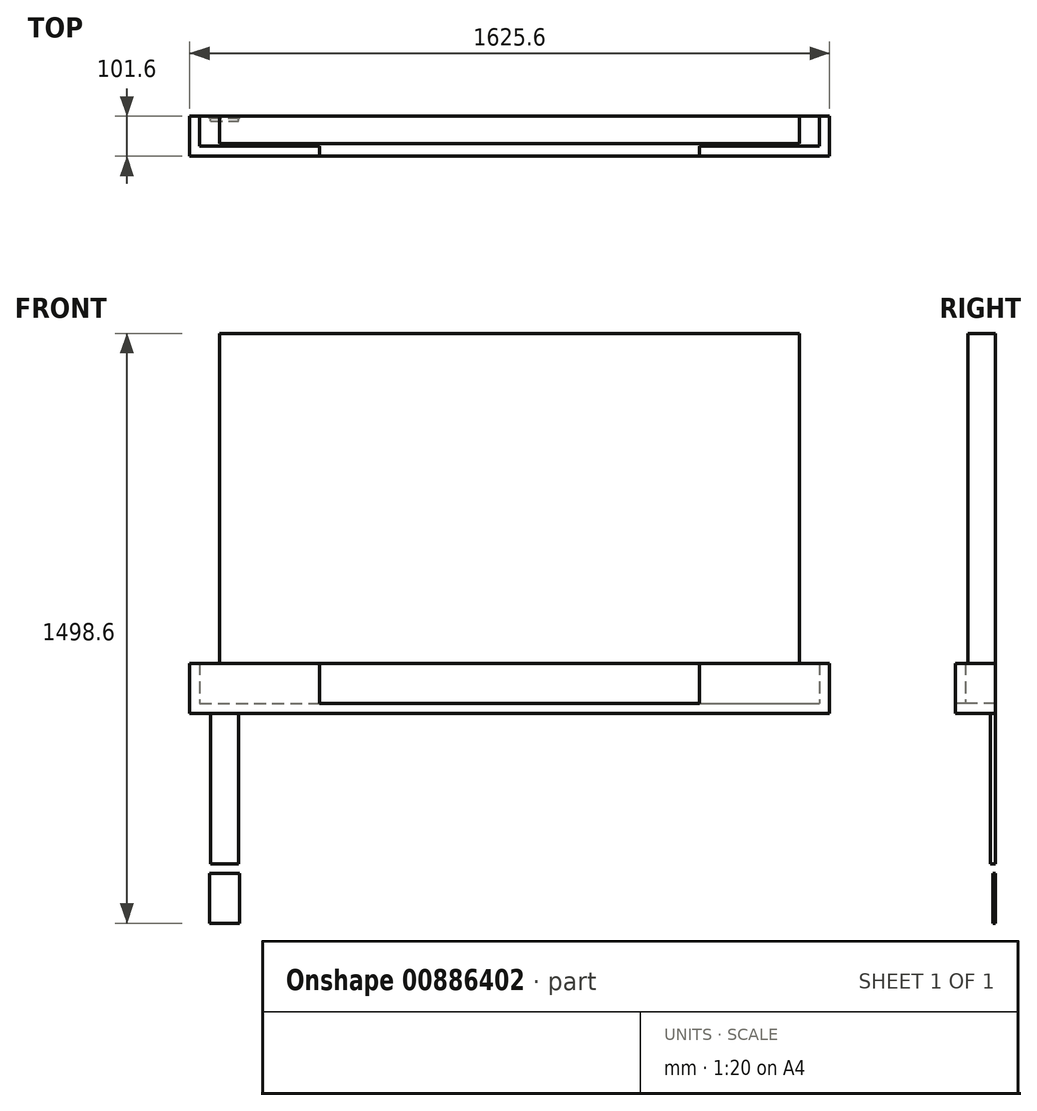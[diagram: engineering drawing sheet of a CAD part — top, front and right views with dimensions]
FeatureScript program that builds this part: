
annotation { "Feature Type Name" : "Feature", "Feature Type Description" : "" }
export const myFeature = defineFeature(function(context is Context, id is Id, definition is map)
    precondition{}
    {
        {
            var Q0;
            Q0=qCreatedBy(makeId("Top.planeOp"),FACE);
            var sketch = newSketch(context, id + "F0", { "sketchPlane" : qUnion([Q0])});
            skLineSegment(sketch, "E0.bottom", {"start": v(0, 0) * mm, "end": v(1625.6, 0) * mm});
            skLineSegment(sketch, "E0.top", {"start": v(0, -101.6) * mm, "end": v(1625.6, -101.6) * mm});
            skLineSegment(sketch, "E0.left", {"start": v(0, 0) * mm, "end": v(0, -101.6) * mm});
            skLineSegment(sketch, "E0.right", {"start": v(1625.6, 0) * mm, "end": v(1625.6, -101.6) * mm});
            skSolve(sketch);
        }
        {
            var Q0;
            Q0 = qSketchRegion(id + "F0", true);
            extrude(context, id + "F1", {"entities" : qUnion([Q0]), "depth" : 25.4 * mm, "offsetDistance" : 25.4 * mm});
        }
        {
            var Q0;
            Q0=makeQuery(id+"F1.opExtrude","CAP_FACE",FACE,{"disambiguationData":[OSD([sQuery(id+"F0.wireOp",EDGE,"E0.bottom"),sQuery(id+"F0.wireOp",EDGE,"E0.top"),sQuery(id+"F0.wireOp",EDGE,"E0.left"),sQuery(id+"F0.wireOp",EDGE,"E0.right")])],"isStart":false});
            var sketch = newSketch(context, id + "F2", { "sketchPlane" : qUnion([Q0])});
            skLineSegment(sketch, "E1.bottom", {"start": v(0, -76.2) * mm, "end": v(1625.6, -76.2) * mm});
            skLineSegment(sketch, "E1.top", {"start": v(0, -101.6) * mm, "end": v(1625.6, -101.6) * mm});
            skLineSegment(sketch, "E1.left", {"start": v(0, -76.2) * mm, "end": v(0, -101.6) * mm});
            skLineSegment(sketch, "E1.right", {"start": v(1625.6, -76.2) * mm, "end": v(1625.6, -101.6) * mm});
            skSolve(sketch);
        }
        {
            var Q0;
            Q0 = qSketchRegion(id + "F2", true);
            extrude(context, id + "F3", {"entities" : qUnion([Q0]), "operationType" : NewBodyOperationType.ADD, "depth" : 101.6 * mm, "offsetDistance" : 25.4 * mm});
        }
        {
            var Q0;
            Q0=makeQuery(id+"F1.opExtrude","CAP_FACE",FACE,{"disambiguationData":[OSD([sQuery(id+"F0.wireOp",EDGE,"E0.bottom"),sQuery(id+"F0.wireOp",EDGE,"E0.top"),sQuery(id+"F0.wireOp",EDGE,"E0.left"),sQuery(id+"F0.wireOp",EDGE,"E0.right")])],"isStart":false});
            var sketch = newSketch(context, id + "F4", { "sketchPlane" : qUnion([Q0])});
            skLineSegment(sketch, "E2.bottom", {"start": v(0, 0) * mm, "end": v(25.4, 0) * mm});
            skLineSegment(sketch, "E2.top", {"start": v(0, -76.2) * mm, "end": v(25.4, -76.2) * mm});
            skLineSegment(sketch, "E2.left", {"start": v(0, 0) * mm, "end": v(0, -76.2) * mm});
            skLineSegment(sketch, "E2.right", {"start": v(25.4, 0) * mm, "end": v(25.4, -76.2) * mm});
            skLineSegment(sketch, "E3.bottom", {"start": v(1625.6, 0) * mm, "end": v(1600.2, 0) * mm});
            skLineSegment(sketch, "E3.top", {"start": v(1625.6, -76.2) * mm, "end": v(1600.2, -76.2) * mm});
            skLineSegment(sketch, "E3.left", {"start": v(1625.6, 0) * mm, "end": v(1625.6, -76.2) * mm});
            skLineSegment(sketch, "E3.right", {"start": v(1600.2, 0) * mm, "end": v(1600.2, -76.2) * mm});
            skSolve(sketch);
        }
        {
            var Q0;
            Q0 = qSketchRegion(id + "F4", true);
            extrude(context, id + "F5", {"entities" : qUnion([Q0]), "operationType" : NewBodyOperationType.ADD, "depth" : 101.6 * mm, "offsetDistance" : 25.4 * mm});
        }
        {
            var Q0;
            Q0=makeQuery(id+"F3.boolean.opBoolean","MERGE",FACE,{"derivedFrom":[makeQuery(id+"F1.opExtrude","SWEPT_FACE",FACE,{"disambiguationData":[OSD([sQuery(id+"F0.wireOp",EDGE,"E0.top")])]}),makeQuery(id+"F3.opExtrude","SWEPT_FACE",FACE,{"disambiguationData":[OSD([sQuery(id+"F2.wireOp",EDGE,"E1.top")])]})]});
            var sketch = newSketch(context, id + "F6", { "sketchPlane" : qUnion([Q0])});
            skLineSegment(sketch, "E4.bottom", {"start": v(330.2, 127) * mm, "end": v(1295.4, 127) * mm});
            skLineSegment(sketch, "E4.top", {"start": v(330.2, 25.4) * mm, "end": v(1295.4, 25.4) * mm});
            skLineSegment(sketch, "E4.left", {"start": v(330.2, 127) * mm, "end": v(330.2, 25.4) * mm});
            skLineSegment(sketch, "E4.right", {"start": v(1295.4, 127) * mm, "end": v(1295.4, 25.4) * mm});
            skSolve(sketch);
        }
        {
            var Q0;
            Q0 = qSketchRegion(id + "F6", true);
            extrude(context, id + "F7", {"entities" : qUnion([Q0]), "operationType" : NewBodyOperationType.REMOVE, "oppositeDirection" : true, "depth" : 25.4 * mm, "offsetDistance" : 25.4 * mm});
        }
        {
            var Q0;
            {var subQ0=sQuery(id+"F4.wireOp",EDGE,"E2.left");var subQ1=sQuery(id+"F4.wireOp",EDGE,"E2.bottom");var subQ2=sQuery(id+"F2.wireOp",EDGE,"E1.left");var subQ3=sQuery(id+"F4.wireOp",EDGE,"E2.right");var subQ4=sQuery(id+"F4.wireOp",EDGE,"E3.bottom");var subQ5=sQuery(id+"F2.wireOp",EDGE,"E1.bottom");var subQ6=sQuery(id+"F2.wireOp",EDGE,"E1.top");Q0=makeQuery(id+"F7.boolean.opBoolean","SPLIT",FACE,{"disambiguationData":[TD([makeQuery(id+"F1.opExtrude","SWEPT_FACE",FACE,{"disambiguationData":[OSD([sQuery(id+"F0.wireOp",EDGE,"E0.left")])]})])],"derivedFrom":makeQuery(id+"F5.boolean.opBoolean","MERGE",FACE,{"derivedFrom":[makeQuery(id+"F3.opExtrude","CAP_FACE",FACE,{"disambiguationData":[OSD([subQ5,subQ6,subQ2,sQuery(id+"F2.wireOp",EDGE,"E1.right")])],"isStart":false}),makeQuery(id+"F5.opExtrude","CAP_FACE",FACE,{"disambiguationData":[OSD([subQ1,sQuery(id+"F4.wireOp",EDGE,"E2.top"),subQ0,subQ3])],"isStart":false}),makeQuery(id+"F5.opExtrude","CAP_FACE",FACE,{"disambiguationData":[OSD([subQ4,sQuery(id+"F4.wireOp",EDGE,"E3.top"),sQuery(id+"F4.wireOp",EDGE,"E3.left"),sQuery(id+"F4.wireOp",EDGE,"E3.right")])],"isStart":false})]})});}
            var sketch = newSketch(context, id + "F8", { "sketchPlane" : qUnion([Q0])});
            skLineSegment(sketch, "E5.bottom", {"start": v(76.2, 0) * mm, "end": v(1549.4, 0) * mm});
            skLineSegment(sketch, "E5.top", {"start": v(76.2, -69.85) * mm, "end": v(1549.4, -69.85) * mm});
            skLineSegment(sketch, "E5.left", {"start": v(76.2, 0) * mm, "end": v(76.2, -69.85) * mm});
            skLineSegment(sketch, "E5.right", {"start": v(1549.4, 0) * mm, "end": v(1549.4, -69.85) * mm});
            skSolve(sketch);
        }
        {
            var Q0;
            Q0 = qSketchRegion(id + "F8", true);
            extrude(context, id + "F9", {"entities" : qUnion([Q0]), "depth" : 838.2 * mm, "offsetDistance" : 25.4 * mm});
        }
        {
            var Q0;
            Q0=makeQuery(id+"F5.boolean.opBoolean","MERGE",FACE,{"derivedFrom":[makeQuery(id+"F1.opExtrude","SWEPT_FACE",FACE,{"disambiguationData":[OSD([sQuery(id+"F0.wireOp",EDGE,"E0.bottom")])]}),makeQuery(id+"F5.opExtrude","SWEPT_FACE",FACE,{"disambiguationData":[OSD([sQuery(id+"F4.wireOp",EDGE,"E2.bottom")])]}),makeQuery(id+"F5.opExtrude","SWEPT_FACE",FACE,{"disambiguationData":[OSD([sQuery(id+"F4.wireOp",EDGE,"E3.bottom")])]})]});
            var sketch = newSketch(context, id + "F10", { "sketchPlane" : qUnion([Q0])});
            skLineSegment(sketch, "E6.bottom", {"start": v(-127, -406.4) * mm, "end": v(-50.8, -406.4) * mm});
            skLineSegment(sketch, "E6.top", {"start": v(-127, -533.4) * mm, "end": v(-50.8, -533.4) * mm});
            skLineSegment(sketch, "E6.left", {"start": v(-127, -406.4) * mm, "end": v(-127, -533.4) * mm});
            skLineSegment(sketch, "E6.right", {"start": v(-50.8, -406.4) * mm, "end": v(-50.8, -533.4) * mm});
            skSolve(sketch);
        }
        {
            var Q0;
            Q0=makeQuery(id+"F10.imprint","IMPRINT",FACE,{"disambiguationData":[TD([[makeQuery(id+"F10.imprint","IMPRINT",EDGE,{"derivedFrom":sQuery(id+"F10.wireOp",EDGE,"E6.bottom")}),-1.0]])]});
            extrude(context, id + "F11", {"entities" : qUnion([Q0]), "oppositeDirection" : true, "depth" : 6.35 * mm, "offsetDistance" : 25.4 * mm});
        }
        {
            var Q0;
            Q0=qCreatedBy(makeId("Front.planeOp"),FACE);
            var sketch = newSketch(context, id + "F12", { "sketchPlane" : qUnion([Q0])});
            skLineSegment(sketch, "E7.bottom", {"start": v(53.1, 0) * mm, "end": v(124.2, 0) * mm});
            skLineSegment(sketch, "E7.top", {"start": v(53.1, -382.47) * mm, "end": v(124.2, -382.47) * mm});
            skLineSegment(sketch, "E7.left", {"start": v(53.1, 0) * mm, "end": v(53.1, -382.47) * mm});
            skLineSegment(sketch, "E7.right", {"start": v(124.2, 0) * mm, "end": v(124.2, -382.47) * mm});
            skSolve(sketch);
        }
        {
            var Q0;
            Q0 = qSketchRegion(id + "F12", true);
            extrude(context, id + "F13", {"entities" : qUnion([Q0]), "operationType" : NewBodyOperationType.ADD, "depth" : 12.7 * mm, "offsetDistance" : 25.4 * mm});
        }
    });
